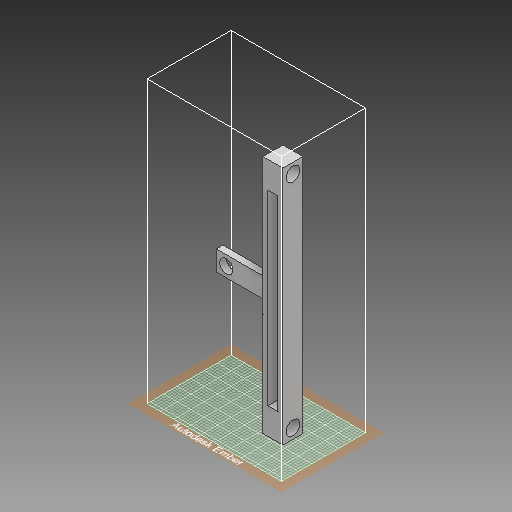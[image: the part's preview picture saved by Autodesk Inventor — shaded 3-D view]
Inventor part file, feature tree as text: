
AUTODESK INVENTOR PART (.ipt)
format: ipt  version: 2018 (Build 220112000, 112)  size: 333,824 bytes
history: native  units: in
note: dims shown in document units (in); Inventor stores cm internally (conversion verified against a paired STEP export)
features: sketch x19, extrude x9, fillet x2, hole x1
ambient origin geometry x8: Origin, YZ Plane, XZ Plane, XY Plane, X Axis, Y Axis, Z Axis, Center Point
bodies: Solid1 (feature_tree)
feature tree (31):
  extrude  "Extrusion1"  Depth=4.5in
  sketch  "Sketch2"  dims[d2=0.375in d3=0.0in d4=0.1875in]
  extrude  "Extrusion2"  Depth=0.1875in
  extrude  "Extrusion3"  Depth=0.375in TaperAngle=0.0deg
  sketch  "Sketch5"  dims[d10=0.325in d11=0.0in d12=0.3625in d13=0.0in]
  extrude  "Extrusion4"  Depth=0.25in
  extrude  "Extrusion5"  Depth=0.3625in TaperAngle=0.0deg
  extrude  "Extrusion6"  Depth=0.26in
  sketch  "Sketch9"  dims[d25=0.25in d26=0.0in d27=0.125in]
  sketch  "Sketch10"  dims[d28=0.125in d29=1.0in]
  extrude  "Extrusion7"  Depth=0.375in
  sketch  "Sketch12"  dims[d31=0.125in d32=0.0in]
  extrude  "Extrusion8"  Depth=0.25in TaperAngle=0.0deg
  fillet  "Fillet1"  Radius=0.25in
  fillet  "Fillet2"  Radius=0.25in
  sketch  "Sketch14"  dims[d39=0.8108in]
  sketch  "Sketch15"
  sketch  "Sketch16"
  sketch  "Sketch17"
  sketch  "Sketch18"
  sketch  "Sketch19"
  extrude  "Extrusion9"  Depth=0.125in
  hole  "Hole1"  [1 undecoded]
  sketch  "Sketch1"  dims[d0=0.375in d1=4.5in]
  sketch  "Sketch3"  dims[d5=3.5in d6=0.375in d7=0.0in]
  sketch  "Sketch4"  dims[d8=0.25in d9=0.26in]
  sketch  "Sketch6"  dims[d14=0.26in d15=0.26in]
  sketch  "Sketch7"  dims[d16=0.3in d17=0.0in d18=0.375in]
  sketch  "Sketch8"  dims[d19=0.125in d20=0.75in d21=0.0in d22=0.25in d23=0.0in d24=0.25in]
  sketch  "Sketch11"  dims[d30=1.0in]
  sketch  "Sketch13"  dims[d33=0.25in d34=0.75in d35=0.375in d36=0.25in d37=0.5635in d38=0.12in]
note: 1 required parameter value undecoded (feature->parameter linkage not recoverable at this tier; creation-order binding heuristic only, values carry confidence <= 0.55)
